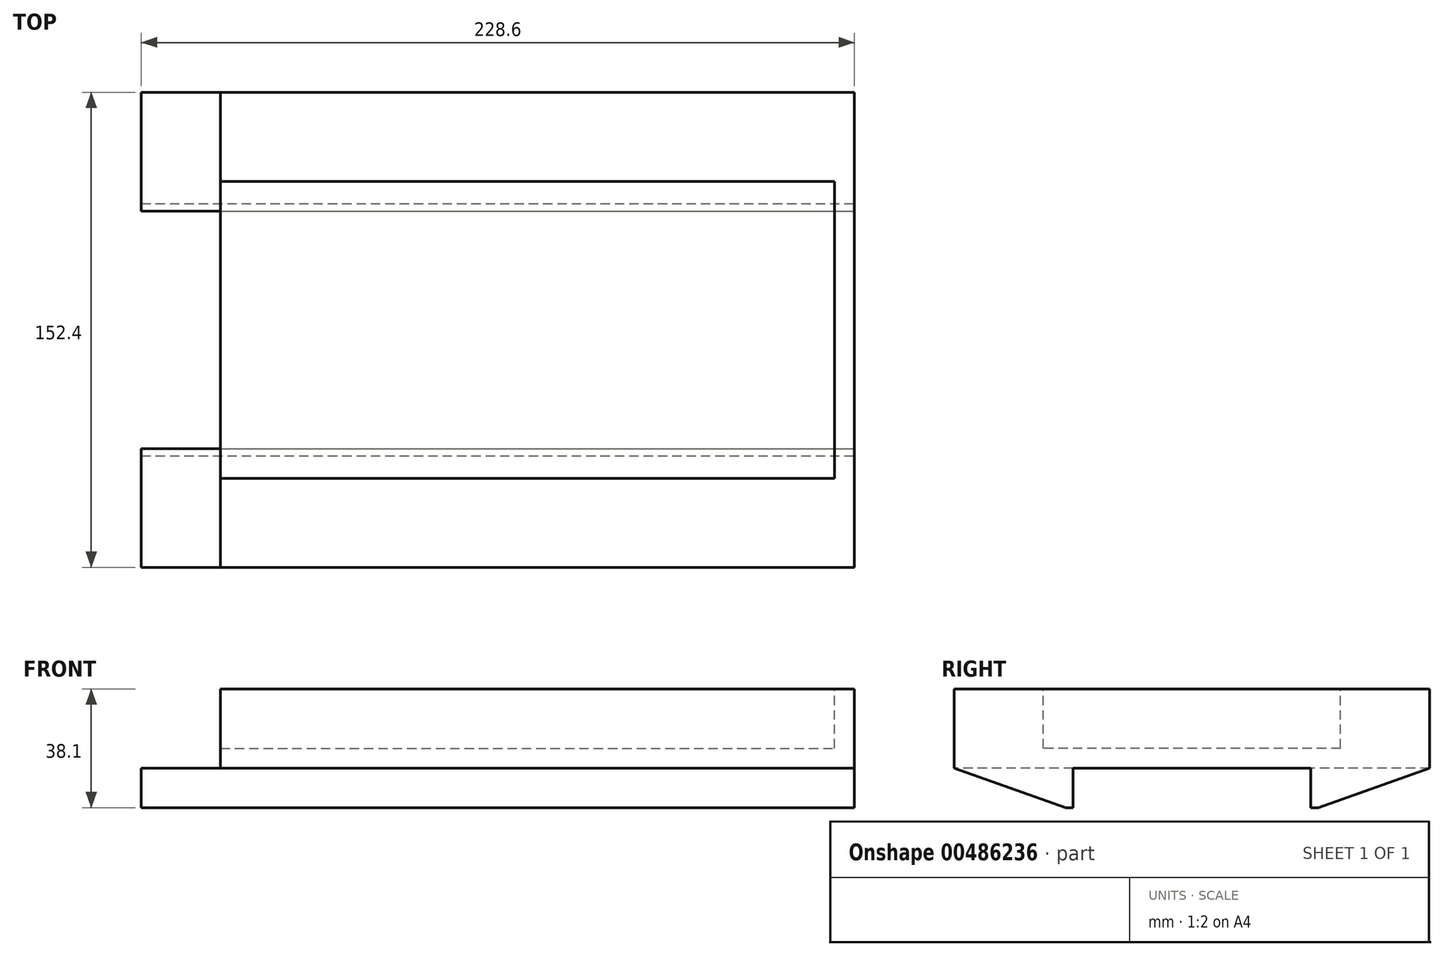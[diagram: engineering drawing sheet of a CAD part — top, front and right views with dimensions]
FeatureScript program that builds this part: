
annotation { "Feature Type Name" : "Feature", "Feature Type Description" : "" }
export const myFeature = defineFeature(function(context is Context, id is Id, definition is map)
    precondition{}
    {
        {
            var Q0;
            Q0=qCreatedBy(makeId("Top.planeOp"),FACE);
            var sketch = newSketch(context, id + "F0", { "sketchPlane" : qUnion([Q0])});
            skLineSegment(sketch, "E0.bottom", {"start": v(101.6, 76.2) * mm, "end": v(-101.6, 76.2) * mm});
            skLineSegment(sketch, "E0.top", {"start": v(101.6, -76.2) * mm, "end": v(-101.6, -76.2) * mm});
            skLineSegment(sketch, "E0.left", {"start": v(101.6, 76.2) * mm, "end": v(101.6, -76.2) * mm});
            skLineSegment(sketch, "E0.right", {"start": v(-101.6, 76.2) * mm, "end": v(-101.6, -76.2) * mm});
            skPoint(sketch, "E0.middle", {"position": v(0, 0) * mm});
            skSolve(sketch);
        }
        {
            var Q0;
            Q0=makeQuery(id+"F0.imprint","IMPRINT",FACE,{"disambiguationData":[TD([[makeQuery(id+"F0.imprint","IMPRINT",EDGE,{"derivedFrom":sQuery(id+"F0.wireOp",EDGE,"E0.bottom")}),1.0]])]});
            extrude(context, id + "F1", {"entities" : qUnion([Q0]), "depth" : 25.4 * mm, "offsetDistance" : 25.4 * mm});
        }
        {
            var Q0;
            Q0=makeQuery(id+"F1.opExtrude","SWEPT_FACE",FACE,{"disambiguationData":[OSD([sQuery(id+"F0.wireOp",EDGE,"E0.left")])]});
            var sketch = newSketch(context, id + "F2", { "sketchPlane" : qUnion([Q0])});
            skLineSegment(sketch, "E1", {"start": v(0, 0) * mm, "end": v(38.1, 0) * mm, "construction": true});
            skLineSegment(sketch, "E2", {"start": v(38.1, 0) * mm, "end": v(-38.1, 0) * mm, "construction": true});
            skLineSegment(sketch, "E3", {"start": v(-38.1, 0) * mm, "end": v(-38.1, -12.7) * mm});
            skLineSegment(sketch, "E4", {"start": v(-38.1, -12.7) * mm, "end": v(-40.43, -12.7) * mm});
            skLineSegment(sketch, "E5", {"start": v(-76.2, 0) * mm, "end": v(-40.43, -12.7) * mm});
            skLineSegment(sketch, "E6", {"start": v(0, 0) * mm, "end": v(0, -35.45) * mm, "construction": true});
            skLineSegment(sketch, "E7.MirrorCS", {"start": v(38.1, 0) * mm, "end": v(38.1, -12.7) * mm});
            skLineSegment(sketch, "E8.MirrorCS", {"start": v(76.2, 0) * mm, "end": v(40.43, -12.7) * mm});
            skLineSegment(sketch, "E9.MirrorCS", {"start": v(38.1, -12.7) * mm, "end": v(40.43, -12.7) * mm});
            skLineSegment(sketch, "E10", {"start": v(-76.2, 0) * mm, "end": v(76.2, 0) * mm});
            skSolve(sketch);
        }
        {
            var Q0;
            Q0 = qSketchRegion(id + "F2", true);
            extrude(context, id + "F3", {"entities" : qUnion([Q0]), "operationType" : NewBodyOperationType.ADD, "oppositeDirection" : true, "depth" : 177.8 * mm, "offsetDistance" : 25.4 * mm});
        }
        {
            var Q0;
            Q0=makeQuery(id+"F1.opExtrude","CAP_FACE",FACE,{"disambiguationData":[OSD([sQuery(id+"F0.wireOp",EDGE,"E0.bottom"),sQuery(id+"F0.wireOp",EDGE,"E0.top"),sQuery(id+"F0.wireOp",EDGE,"E0.left"),sQuery(id+"F0.wireOp",EDGE,"E0.right")])],"isStart":false});
            var sketch = newSketch(context, id + "F4", { "sketchPlane" : qUnion([Q0])});
            skLineSegment(sketch, "E11", {"start": v(-101.6, -76.2) * mm, "end": v(-101.6, 76.2) * mm, "construction": true});
            skLineSegment(sketch, "E12", {"start": v(-101.6, 0) * mm, "end": v(-101.6, 38.1) * mm, "construction": true});
            skLineSegment(sketch, "E13", {"start": v(-101.6, 38.1) * mm, "end": v(-101.6, -38.1) * mm, "construction": true});
            skLineSegment(sketch, "E14", {"start": v(-101.6, -38.1) * mm, "end": v(-101.6, -76.2) * mm, "construction": true});
            skLineSegment(sketch, "E15", {"start": v(-101.6, -76.2) * mm, "end": v(-101.6, -38.1) * mm, "construction": true});
            skLineSegment(sketch, "E16", {"start": v(-101.6, -57.15) * mm, "end": v(-101.6, -38.1) * mm, "construction": true});
            skLineSegment(sketch, "E17", {"start": v(-101.6, -47.62) * mm, "end": v(44.45, -47.62) * mm});
            skLineSegment(sketch, "E18", {"start": v(-101.6, 0) * mm, "end": v(-9.81, 0) * mm, "construction": true});
            skLineSegment(sketch, "E19.MirrorCS", {"start": v(-101.6, 47.62) * mm, "end": v(44.45, 47.62) * mm});
            skLineSegment(sketch, "E20", {"start": v(44.45, -47.62) * mm, "end": v(44.45, 47.62) * mm, "construction": true});
            skLineSegment(sketch, "E21", {"start": v(-101.6, -47.62) * mm, "end": v(-101.6, 47.62) * mm, "construction": true});
            skLineSegment(sketch, "E22", {"start": v(44.45, -47.62) * mm, "end": v(44.45, 47.62) * mm});
            skLineSegment(sketch, "E23", {"start": v(-101.6, -47.62) * mm, "end": v(-101.6, 47.62) * mm});
            skSolve(sketch);
        }
        {
            var Q0;
            Q0 = qSketchRegion(id + "F4", true);
            extrude(context, id + "F5", {"entities" : qUnion([Q0]), "operationType" : NewBodyOperationType.REMOVE, "oppositeDirection" : true, "depth" : 19.05 * mm, "offsetDistance" : 25.4 * mm});
        }
        {
            var Q0;
            Q0=makeQuery(id+"F3.opExtrude","CAP_FACE",FACE,{"disambiguationData":[OSD([sQuery(id+"F2.wireOp",EDGE,"E3"),sQuery(id+"F2.wireOp",EDGE,"E4"),sQuery(id+"F2.wireOp",EDGE,"E5"),sQuery(id+"F2.wireOp",EDGE,"E10")])],"isStart":false});
            var Q1;
            Q1=makeQuery(id+"F3.opExtrude","CAP_FACE",FACE,{"disambiguationData":[OSD([sQuery(id+"F2.wireOp",EDGE,"E7.MirrorCS"),sQuery(id+"F2.wireOp",EDGE,"E8.MirrorCS"),sQuery(id+"F2.wireOp",EDGE,"E9.MirrorCS"),sQuery(id+"F2.wireOp",EDGE,"E10")])],"isStart":false});
            extrude(context, id + "F6", {"entities" : qUnion([Q0, Q1]), "operationType" : NewBodyOperationType.ADD, "depth" : 50.8 * mm, "offsetDistance" : 25.4 * mm});
        }
        {
            var Q0;
            Q0=makeQuery(id+"F1.opExtrude","CAP_FACE",FACE,{"disambiguationData":[OSD([sQuery(id+"F0.wireOp",EDGE,"E0.bottom"),sQuery(id+"F0.wireOp",EDGE,"E0.top"),sQuery(id+"F0.wireOp",EDGE,"E0.left"),sQuery(id+"F0.wireOp",EDGE,"E0.right")])],"isStart":false});
            var sketch = newSketch(context, id + "F7", { "sketchPlane" : qUnion([Q0])});
            skLineSegment(sketch, "E24", {"start": v(101.6, 47.62) * mm, "end": v(95.25, 47.62) * mm});
            skLineSegment(sketch, "E25.bottom", {"start": v(95.25, 47.62) * mm, "end": v(44.45, 47.62) * mm});
            skLineSegment(sketch, "E25.top", {"start": v(95.25, -47.62) * mm, "end": v(44.45, -47.62) * mm});
            skLineSegment(sketch, "E25.left", {"start": v(95.25, 47.62) * mm, "end": v(95.25, -47.62) * mm});
            skLineSegment(sketch, "E25.right", {"start": v(44.45, 47.62) * mm, "end": v(44.45, -47.62) * mm});
            skSolve(sketch);
        }
        {
            var Q0;
            Q0 = qSketchRegion(id + "F7", true);
            extrude(context, id + "F8", {"entities" : qUnion([Q0]), "operationType" : NewBodyOperationType.REMOVE, "oppositeDirection" : true, "depth" : 19.05 * mm, "offsetDistance" : 25.4 * mm});
        }
    });
